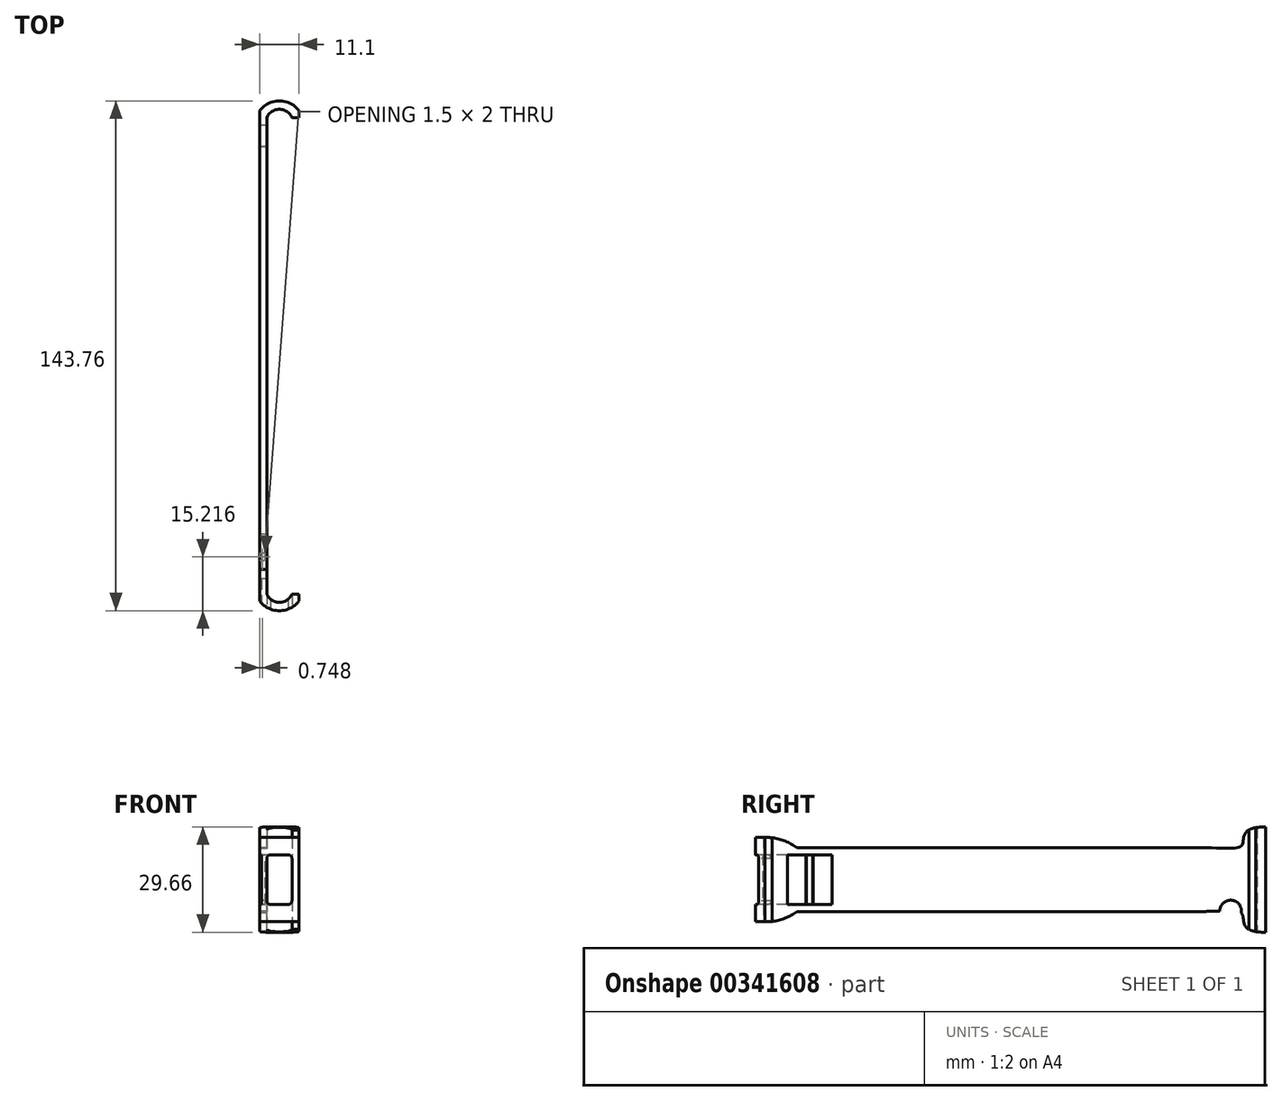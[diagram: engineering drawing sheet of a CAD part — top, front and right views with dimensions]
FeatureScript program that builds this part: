
annotation { "Feature Type Name" : "Feature", "Feature Type Description" : "" }
export const myFeature = defineFeature(function(context is Context, id is Id, definition is map)
    precondition{}
    {
        {
            var Q0;
            Q0=qCreatedBy(makeId("Top.planeOp"),FACE);
            var sketch = newSketch(context, id + "F0", { "sketchPlane" : qUnion([Q0])});
            skLineSegment(sketch, "E0", {"start": v(-2.55, -2.3) * mm, "end": v(-2.55, 64.86) * mm});
            skArc(sketch, "E1", {"start": v(4.55, 64.86) * mm, "mid": v(1, 67.23) * mm, "end": v(-2.55, 64.86) * mm});
            skLineSegment(sketch, "E2.MirrorCS", {"start": v(-2.55, -2.3) * mm, "end": v(-2.55, -69.44) * mm});
            skArc(sketch, "E3.MirrorCS", {"start": v(4.55, -69.44) * mm, "mid": v(1, -71.82) * mm, "end": v(-2.55, -69.44) * mm});
            skLineSegment(sketch, "E4", {"start": v(-4.55, 64.86) * mm, "end": v(-4.55, -2.3) * mm});
            skLineSegment(sketch, "E5", {"start": v(-4.55, 64.86) * mm, "end": v(-4.55, 66.86) * mm});
            skLineSegment(sketch, "E6", {"start": v(4.55, 64.86) * mm, "end": v(6.55, 64.86) * mm});
            skLineSegment(sketch, "E7", {"start": v(6.55, 64.86) * mm, "end": v(6.55, 66.86) * mm});
            skArc(sketch, "E8", {"start": v(6.55, 66.86) * mm, "mid": v(1, 69.59) * mm, "end": v(-4.55, 66.86) * mm});
            skLineSegment(sketch, "E9.MirrorCS", {"start": v(-4.55, -69.44) * mm, "end": v(-4.55, -2.3) * mm});
            skArc(sketch, "E10.MirrorCS", {"start": v(6.55, -71.44) * mm, "mid": v(1, -74.17) * mm, "end": v(-4.55, -71.44) * mm});
            skLineSegment(sketch, "E11.MirrorCS", {"start": v(6.55, -69.44) * mm, "end": v(6.55, -71.44) * mm});
            skLineSegment(sketch, "E12.MirrorCS", {"start": v(-4.55, -69.44) * mm, "end": v(-4.55, -71.44) * mm});
            skLineSegment(sketch, "E13.MirrorCS", {"start": v(4.55, -69.44) * mm, "end": v(6.55, -69.44) * mm});
            skLineSegment(sketch, "E14", {"start": v(-3.8, 66.85) * mm, "end": v(-3.8, 48.8) * mm, "construction": true});
            skCircle(sketch, "E15", {"center": v(-3.8, 57.83) * mm, "radius": 0.75 * mm});
            skLineSegment(sketch, "E16", {"start": v(-1.88, 57.89) * mm, "end": v(-7.74, 57.83) * mm, "construction": true});
            skSolve(sketch);
        }
        {
            var Q0;
            Q0 = qSketchRegion(id + "F0", true);
            extrude(context, id + "F1", {"entities" : qUnion([Q0]), "depth" : 40 * mm, "offsetDistance" : 25 * mm});
        }
        {
            var Q0;
            Q0=qCreatedBy(makeId("Right.planeOp"),FACE);
            cPlane(context, id + "F2", {"entities" : qUnion([Q0]), "cplaneType" : CPlaneType.OFFSET, "offset" : 5 * mm, "oppositeDirection" : true, "width" : 150 * mm, "height" : 150 * mm});
        }
        {
            var Q0;
            Q0=qCreatedBy(id+"F2.planeOp",FACE);
            var sketch = newSketch(context, id + "F3", { "sketchPlane" : qUnion([Q0])});
            skLineSegment(sketch, "E17", {"start": v(-70.66, 18.78) * mm, "end": v(78.5, 18.78) * mm, "construction": true});
            skLineSegment(sketch, "E18", {"start": v(-70.66, 18.78) * mm, "end": v(-96.8, 18.78) * mm, "construction": true});
            skFitSpline(sketch, "E19", {"points": [v(71.91, 33.47) * mm, v(63.2, 29) * mm, v(48.98, 27.78) * mm], "startDerivative": vector(-63.52, 5.97) * mm, "endDerivative": vector(-57.31, -0.18) * mm});
            skLineSegment(sketch, "E20", {"start": v(48.98, 27.78) * mm, "end": v(-62.5, 27.78) * mm});
            skArc(sketch, "E21", {"start": v(-62.5, 27.78) * mm, "mid": v(-66.52, 29.93) * mm, "end": v(-71.03, 30.65) * mm});
            skLineSegment(sketch, "E22", {"start": v(-71.03, 30.65) * mm, "end": v(-77.43, 30.62) * mm});
            skLineSegment(sketch, "E23", {"start": v(-77.43, 30.62) * mm, "end": v(-77.56, 52.76) * mm});
            skLineSegment(sketch, "E24", {"start": v(-77.56, 52.76) * mm, "end": v(72, 52.76) * mm});
            skLineSegment(sketch, "E25", {"start": v(72, 52.76) * mm, "end": v(71.91, 33.47) * mm});
            skFitSpline(sketch, "E26.MirrorCS", {"points": [v(71.91, 4.09) * mm, v(63.2, 8.56) * mm, v(48.98, 9.78) * mm], "startDerivative": vector(-63.52, -5.97) * mm, "endDerivative": vector(-57.31, 0.18) * mm});
            skLineSegment(sketch, "E27.MirrorCS", {"start": v(72, -15.2) * mm, "end": v(71.91, 4.09) * mm});
            skLineSegment(sketch, "E28.MirrorCS", {"start": v(-77.56, -15.2) * mm, "end": v(72, -15.2) * mm});
            skLineSegment(sketch, "E29.MirrorCS", {"start": v(-77.43, 6.94) * mm, "end": v(-77.56, -15.2) * mm});
            skArc(sketch, "E30.MirrorCS", {"start": v(-62.5, 9.78) * mm, "mid": v(-66.52, 7.63) * mm, "end": v(-71.03, 6.9) * mm});
            skLineSegment(sketch, "E31.MirrorCS", {"start": v(-71.03, 6.9) * mm, "end": v(-77.43, 6.94) * mm});
            skLineSegment(sketch, "E32.MirrorCS", {"start": v(48.98, 9.78) * mm, "end": v(-62.5, 9.78) * mm});
            skSolve(sketch);
        }
        {
            var Q0;
            Q0 = qSketchRegion(id + "F3", true);
            extrude(context, id + "F4", {"entities" : qUnion([Q0]), "operationType" : NewBodyOperationType.REMOVE, "depth" : 25 * mm, "offsetDistance" : 25 * mm});
        }
        {
            var Q0;
            Q0=qCreatedBy(id+"F2.planeOp",FACE);
            var sketch = newSketch(context, id + "F5", { "sketchPlane" : qUnion([Q0])});
            skLineSegment(sketch, "E33.bottom", {"start": v(-52.58, 25.78) * mm, "end": v(-101.02, 25.78) * mm});
            skLineSegment(sketch, "E33.top", {"start": v(-52.58, 11.78) * mm, "end": v(-101.02, 11.78) * mm});
            skLineSegment(sketch, "E33.left", {"start": v(-52.58, 25.78) * mm, "end": v(-52.58, 11.78) * mm});
            skLineSegment(sketch, "E33.right", {"start": v(-101.02, 25.78) * mm, "end": v(-101.02, 11.78) * mm});
            skPoint(sketch, "E33.middle", {"position": v(-76.8, 18.78) * mm});
            skLineSegment(sketch, "E34", {"start": v(-52.58, 18.78) * mm, "end": v(-101.02, 18.78) * mm, "construction": true});
            skLineSegment(sketch, "E35.bottom", {"start": v(-52.58, 11.78) * mm, "end": v(-65.2, 11.78) * mm});
            skLineSegment(sketch, "E35.top", {"start": v(-52.58, 25.78) * mm, "end": v(-65.2, 25.78) * mm});
            skLineSegment(sketch, "E35.left", {"start": v(-52.58, 11.78) * mm, "end": v(-52.58, 25.78) * mm});
            skLineSegment(sketch, "E35.right", {"start": v(-65.2, 11.78) * mm, "end": v(-65.2, 25.78) * mm});
            skSolve(sketch);
        }
        {
            var Q0;
            {var subQ3=sQuery(id+"F5.wireOp",EDGE,"E33.left");var subQ7=sQuery(id+"F5.wireOp",EDGE,"E33.right");Q0=qUnion([makeQuery(id+"F5.imprint","IMPRINT",FACE,{"disambiguationData":[TD([[makeQuery(id+"F5.imprint","IMPRINT",EDGE,{"derivedFrom":subQ7}),1.0]])]}),makeQuery(id+"F5.imprint","IMPRINT",FACE,{"disambiguationData":[TD([[makeQuery(id+"F5.imprint","IMPRINT",EDGE,{"derivedFrom":subQ3}),-1.0]])]})]);}
            extrude(context, id + "F6", {"entities" : qUnion([Q0]), "operationType" : NewBodyOperationType.REMOVE, "depth" : 1 * mm, "offsetDistance" : 25 * mm});
        }
        {
            var Q0;
            {var subQ2=sQuery(id+"F5.wireOp",EDGE,"E33.left");Q0=makeQuery(id+"F5.imprint","IMPRINT",FACE,{"disambiguationData":[TD([[makeQuery(id+"F5.imprint","IMPRINT",EDGE,{"derivedFrom":subQ2}),-1.0]])]});}
            extrude(context, id + "F7", {"entities" : qUnion([Q0]), "operationType" : NewBodyOperationType.REMOVE, "depth" : 25 * mm, "offsetDistance" : 25 * mm});
        }
        {
            var Q0;
            Q0=makeQuery(id+"F4.boolean.opBoolean","COPY",FACE,{"derivedFrom":makeQuery(id+"F4.opExtrude","SWEPT_FACE",FACE,{"disambiguationData":[OSD([sQuery(id+"F3.wireOp",EDGE,"E20")])]})});
            var sketch = newSketch(context, id + "F8", { "sketchPlane" : qUnion([Q0])});
            skCircle(sketch, "E36", {"center": v(-3.55, -58.95) * mm, "radius": 1 * mm});
            skLineSegment(sketch, "E37", {"start": v(-3.05, -58.09) * mm, "end": v(-3.05, -59.82) * mm});
            skSolve(sketch);
        }
        {
            var Q0;
            {var subQ0=sQuery(id+"F8.wireOp",EDGE,"E37");Q0=makeQuery(id+"F8.imprint","IMPRINT",FACE,{"disambiguationData":[TD([[makeQuery(id+"F8.imprint","IMPRINT",EDGE,{"derivedFrom":subQ0}),-1.0]])]});}
            extrude(context, id + "F9", {"entities" : qUnion([Q0]), "operationType" : NewBodyOperationType.ADD, "oppositeDirection" : true, "depth" : 18 * mm, "offsetDistance" : 25 * mm});
        }
        {
            var Q0;
            Q0=makeQuery(id+"F1.opExtrude","SWEPT_FACE",FACE,{"disambiguationData":[OSD([sQuery(id+"F0.wireOp",EDGE,"E0"),sQuery(id+"F0.wireOp",EDGE,"E2.MirrorCS")])]});
            var sketch = newSketch(context, id + "F10", { "sketchPlane" : qUnion([Q0])});
            skCircle(sketch, "E38", {"center": v(59.75, 9.93) * mm, "radius": 3.06 * mm});
            skSolve(sketch);
        }
        {
            var Q0;
            Q0 = qSketchRegion(id + "F10", true);
            extrude(context, id + "F11", {"entities" : qUnion([Q0]), "operationType" : NewBodyOperationType.REMOVE, "oppositeDirection" : true, "depth" : 25 * mm, "offsetDistance" : 25 * mm});
        }
        {
            var Q0;
            Q0=qCreatedBy(makeId("Front.planeOp"),FACE);
            cPlane(context, id + "F12", {"entities" : qUnion([Q0]), "cplaneType" : CPlaneType.OFFSET, "offset" : 80 * mm, "width" : 150 * mm, "height" : 150 * mm});
        }
        {
            var Q0;
            Q0=qCreatedBy(id+"F12.planeOp",FACE);
            var sketch = newSketch(context, id + "F13", { "sketchPlane" : qUnion([Q0])});
            skLineSegment(sketch, "E39.bottom", {"start": v(-2.55, 25.77) * mm, "end": v(4.55, 25.77) * mm});
            skLineSegment(sketch, "E39.top", {"start": v(-2.55, 11.77) * mm, "end": v(4.55, 11.77) * mm});
            skLineSegment(sketch, "E39.left", {"start": v(-2.55, 25.77) * mm, "end": v(-2.55, 11.77) * mm});
            skLineSegment(sketch, "E39.right", {"start": v(4.55, 25.77) * mm, "end": v(4.55, 11.77) * mm});
            skArc(sketch, "E40", {"start": v(-1.46, 25.77) * mm, "mid": v(-2.24, 25.45) * mm, "end": v(-2.55, 24.65) * mm});
            skLineSegment(sketch, "E41", {"start": v(-2.55, 18.77) * mm, "end": v(4.55, 18.77) * mm, "construction": true});
            skArc(sketch, "E42.MirrorCS", {"start": v(-1.46, 11.77) * mm, "mid": v(-2.24, 12.1) * mm, "end": v(-2.55, 12.89) * mm});
            skLineSegment(sketch, "E43", {"start": v(1, 25.77) * mm, "end": v(1, 11.77) * mm, "construction": true});
            skArc(sketch, "E44.MirrorCS", {"start": v(3.45, 25.77) * mm, "mid": v(4.24, 25.45) * mm, "end": v(4.55, 24.65) * mm});
            skArc(sketch, "E45.MirrorCS", {"start": v(3.45, 11.77) * mm, "mid": v(4.24, 12.1) * mm, "end": v(4.55, 12.89) * mm});
            skSolve(sketch);
        }
        {
            var Q0;
            {var subQ0=sQuery(id+"F13.wireOp",EDGE,"E40");var subQ1=sQuery(id+"F13.wireOp",EDGE,"E39.bottom");var subQ5=makeQuery(id+"F13.imprint","INTERSECT",VERTEX,{"disambiguationData":[OD(0.0)],"derivedFrom":[subQ1,subQ0]});Q0=makeQuery(id+"F13.imprint","IMPRINT",FACE,{"disambiguationData":[TD([[makeQuery(id+"F13.imprint","IMPRINT",EDGE,{"disambiguationData":[TD([[subQ5,-1.0]])],"derivedFrom":subQ1}),-1.0]])]});}
            extrude(context, id + "F14", {"entities" : qUnion([Q0]), "operationType" : NewBodyOperationType.REMOVE, "oppositeDirection" : true, "depth" : 25 * mm, "offsetDistance" : 25 * mm});
        }
    });
